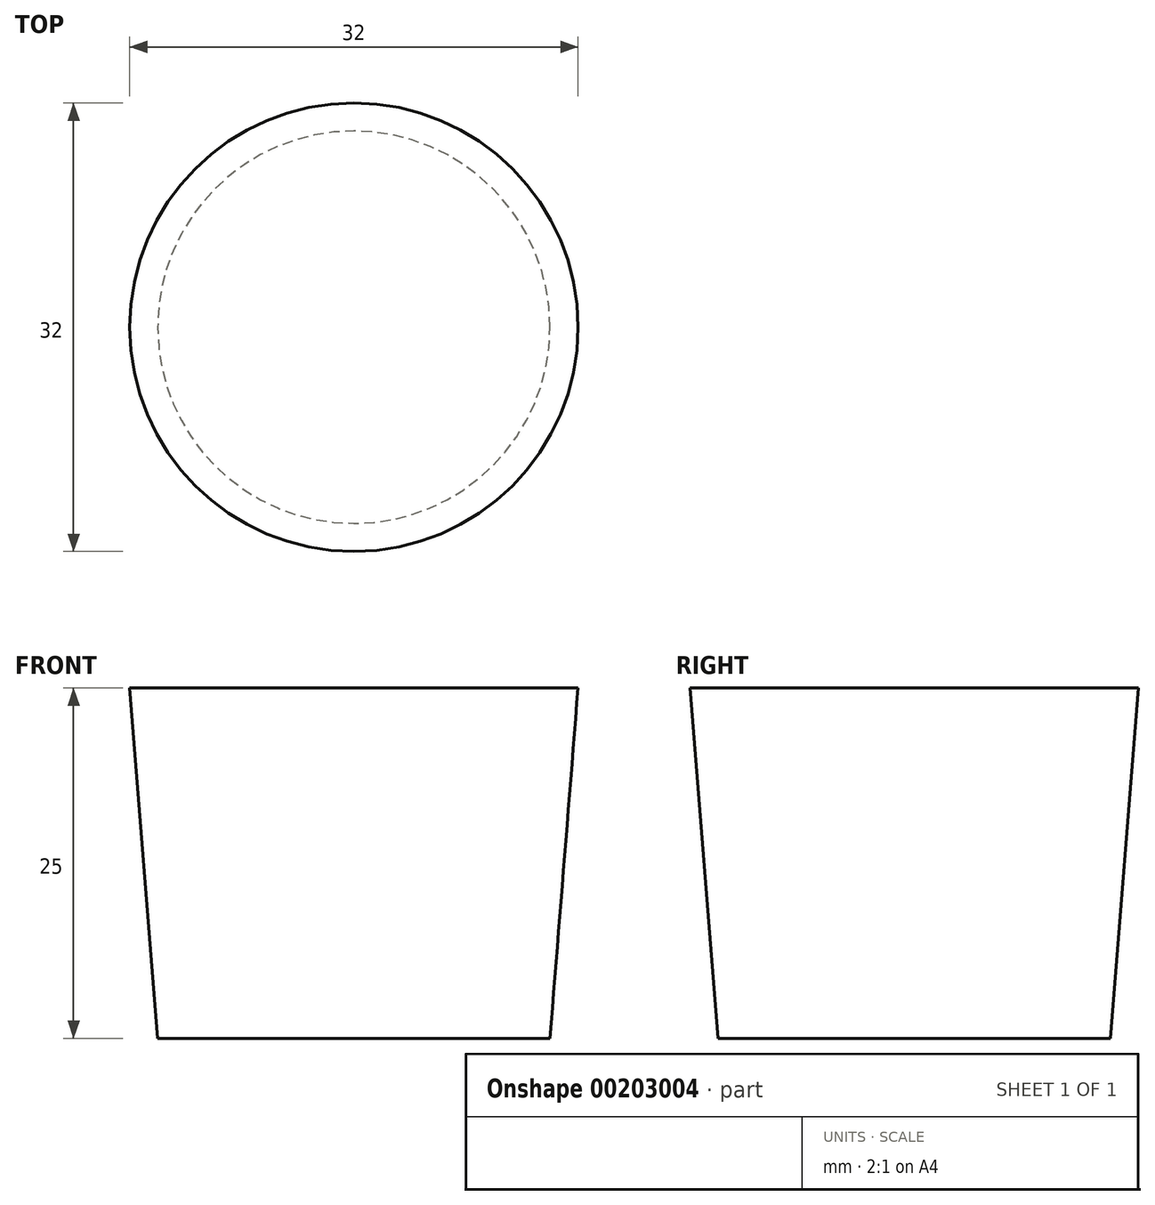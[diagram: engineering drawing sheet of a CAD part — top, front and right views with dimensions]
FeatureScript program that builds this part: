
annotation { "Feature Type Name" : "Feature", "Feature Type Description" : "" }
export const myFeature = defineFeature(function(context is Context, id is Id, definition is map)
    precondition{}
    {
        {
            var Q0;
            Q0=qCreatedBy(makeId("Top.planeOp"),FACE);
            var sketch = newSketch(context, id + "F0", { "sketchPlane" : qUnion([Q0])});
            skCircle(sketch, "E0", {"center": v(0, 0) * mm, "radius": 14 * mm});
            skSolve(sketch);
        }
        {
            var Q0;
            Q0=qCreatedBy(makeId("Top.planeOp"),FACE);
            cPlane(context, id + "F2", {"entities" : qUnion([Q0]), "cplaneType" : CPlaneType.OFFSET, "offset" : 25 * mm, "width" : 150 * mm, "height" : 150 * mm});
        }
        {
            var Q0;
            Q0=qCreatedBy(id+"F2.planeOp",FACE);
            var sketch = newSketch(context, id + "F1", { "sketchPlane" : qUnion([Q0])});
            skPoint(sketch, "E1.0", {"position": v(0, 0) * mm});
            skCircle(sketch, "E2", {"center": v(0, 0) * mm, "radius": 16 * mm});
            skSolve(sketch);
        }
        {
            var Q0;
            Q0=makeQuery(id+"F1.imprint","IMPRINT",FACE,{"disambiguationData":[TD([[makeQuery(id+"F1.imprint","IMPRINT",EDGE,{"derivedFrom":sQuery(id+"F1.wireOp",EDGE,"E2")}),1.0]])]});
            var Q1;
            Q1=makeQuery(id+"F0.imprint","IMPRINT",FACE,{"disambiguationData":[TD([[makeQuery(id+"F0.imprint","IMPRINT",EDGE,{"derivedFrom":sQuery(id+"F0.wireOp",EDGE,"E0")}),1.0]])]});
            loft(context, id + "F3", {"sheetProfilesArray" : [{ "sheetProfileEntities" : qUnion([Q0]) }, { "sheetProfileEntities" : qUnion([Q1]) }]});
        }
    });
